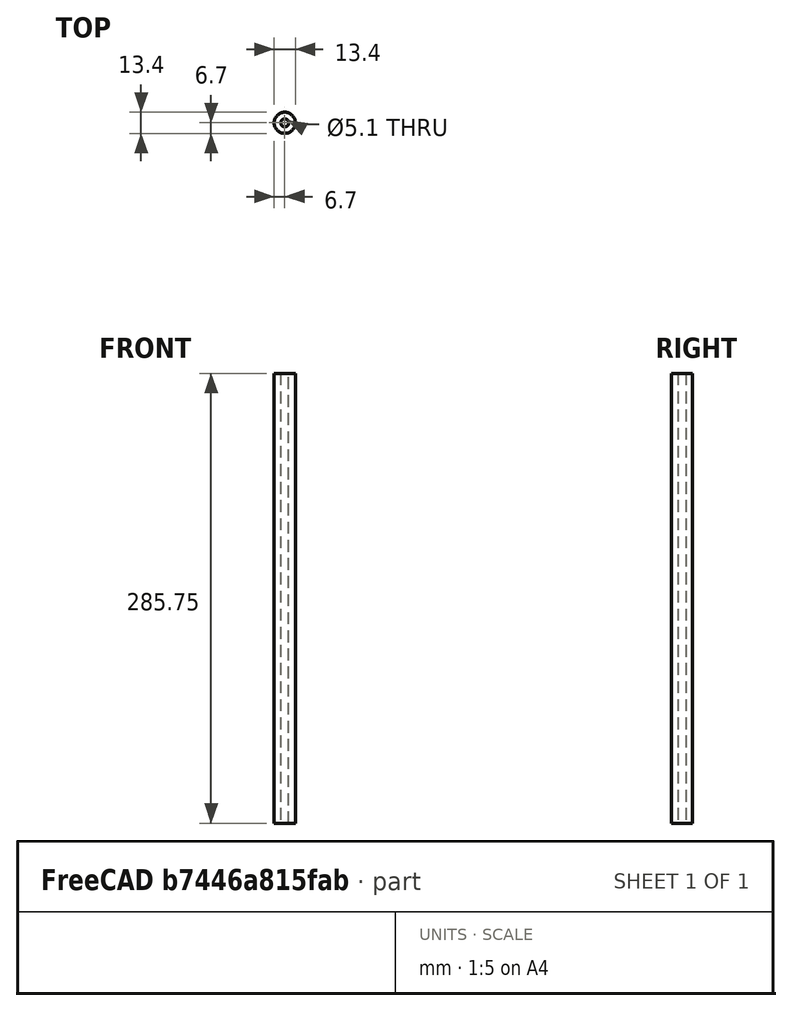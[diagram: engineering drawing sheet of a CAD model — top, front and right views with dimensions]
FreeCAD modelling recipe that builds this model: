
FCSTD DOCUMENT  (FreeCAD 0.20R29603 (Git))
Label: big rod
License: All rights reserved
LicenseURL: http://en.wikipedia.org/wiki/All_rights_reserved
objects: Spreadsheet::Sheet×1, Sketcher::SketchObject×1, PartDesign::Pad×1, PartDesign::Body×1
note: 4 computed .brp shape members not serialized (recipe doc carries the construction recipe); baked Part::Feature solids carry a one-line shape summary decoded from their .brp

FEATURE [Spreadsheet::Sheet] Spreadsheet  label="big_rod_dims"
  cells = A1=big_rod_OD; B1(BIG_ROD_OD)=13.4; A2=big_rod_ID; B2(big_rod_ID)=5.1; A3=big_rod_Length; B3(big_rod_Length)=285.75
FEATURE [Sketcher::SketchObject] Sketch
  FullyConstrained = true
  MapMode = 5
  Support = -> [XY_Plane]
  expr: Constraints[1] = <<big_rod_dims>>.BIG_ROD_OD
  expr: Constraints[3] = <<big_rod_dims>>.big_rod_ID
  sketch-geometry (2):
    g0: Circle CenterX=0 CenterY=0 CenterZ=0 NormalX=0 NormalY=0 NormalZ=1 AngleXU=0 Radius=6.7
    g1: Circle CenterX=0 CenterY=0 CenterZ=0 NormalX=0 NormalY=0 NormalZ=1 AngleXU=0 Radius=2.55
  constraints (4):
    c: Coincident(g0,g-1)
    c: Diameter(g0) = 13.4
    c: Coincident(g1,g0)
    c: Diameter(g1) = 5.1
FEATURE [PartDesign::Pad] Pad
  Direction = (0,0,1)
  Length = 285.75
  Length2 = 10
  Profile = -> Sketch
  ReferenceAxis = -> Sketch [N_Axis]
  Type = 0
  expr: Length = <<big_rod_dims>>.big_rod_Length
FEATURE [PartDesign::Body] Body  label="big rod"
  Group = -> [Sketch,Pad]
  Origin = -> Origin
  Placement = pos=(88,0,0) rot=(0,0,1;0rad)
  Tip = -> Pad
